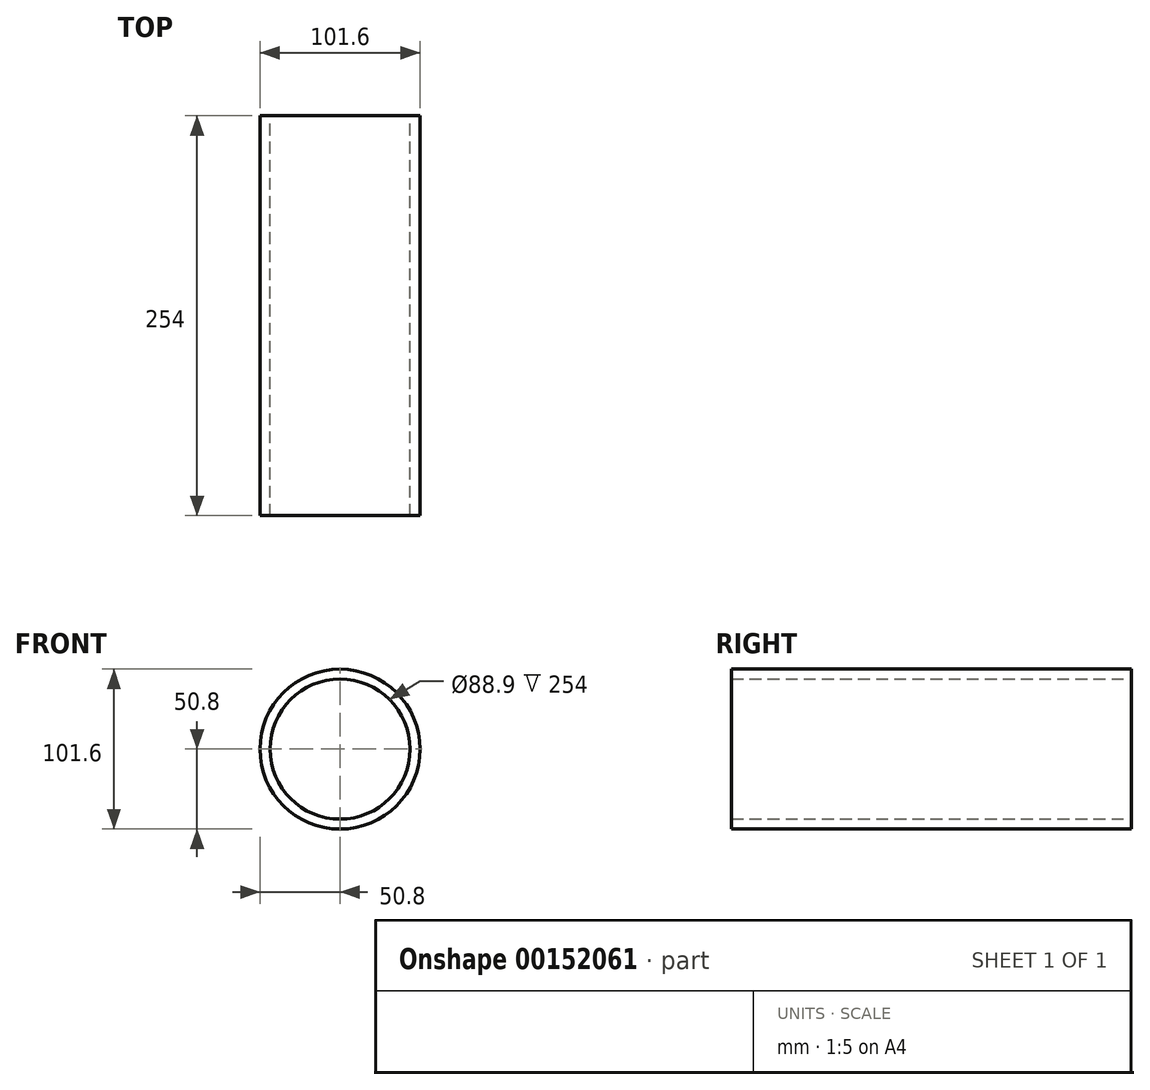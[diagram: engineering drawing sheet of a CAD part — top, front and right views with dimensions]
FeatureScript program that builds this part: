
annotation { "Feature Type Name" : "Feature", "Feature Type Description" : "" }
export const myFeature = defineFeature(function(context is Context, id is Id, definition is map)
    precondition{}
    {
        {
            var Q0;
            Q0=qCreatedBy(makeId("Front.planeOp"),FACE);
            var sketch = newSketch(context, id + "F0", { "sketchPlane" : qUnion([Q0])});
            skCircle(sketch, "E0", {"center": v(0, 0) * mm, "radius": 50.8 * mm});
            skCircle(sketch, "E1", {"center": v(0, 0) * mm, "radius": 44.45 * mm});
            skSolve(sketch);
        }
        {
            var Q0;
            Q0 = qSketchRegion(id + "F0", true);
            extrude(context, id + "F1", {"entities" : qUnion([Q0]), "depth" : 254 * mm});
        }
    });
